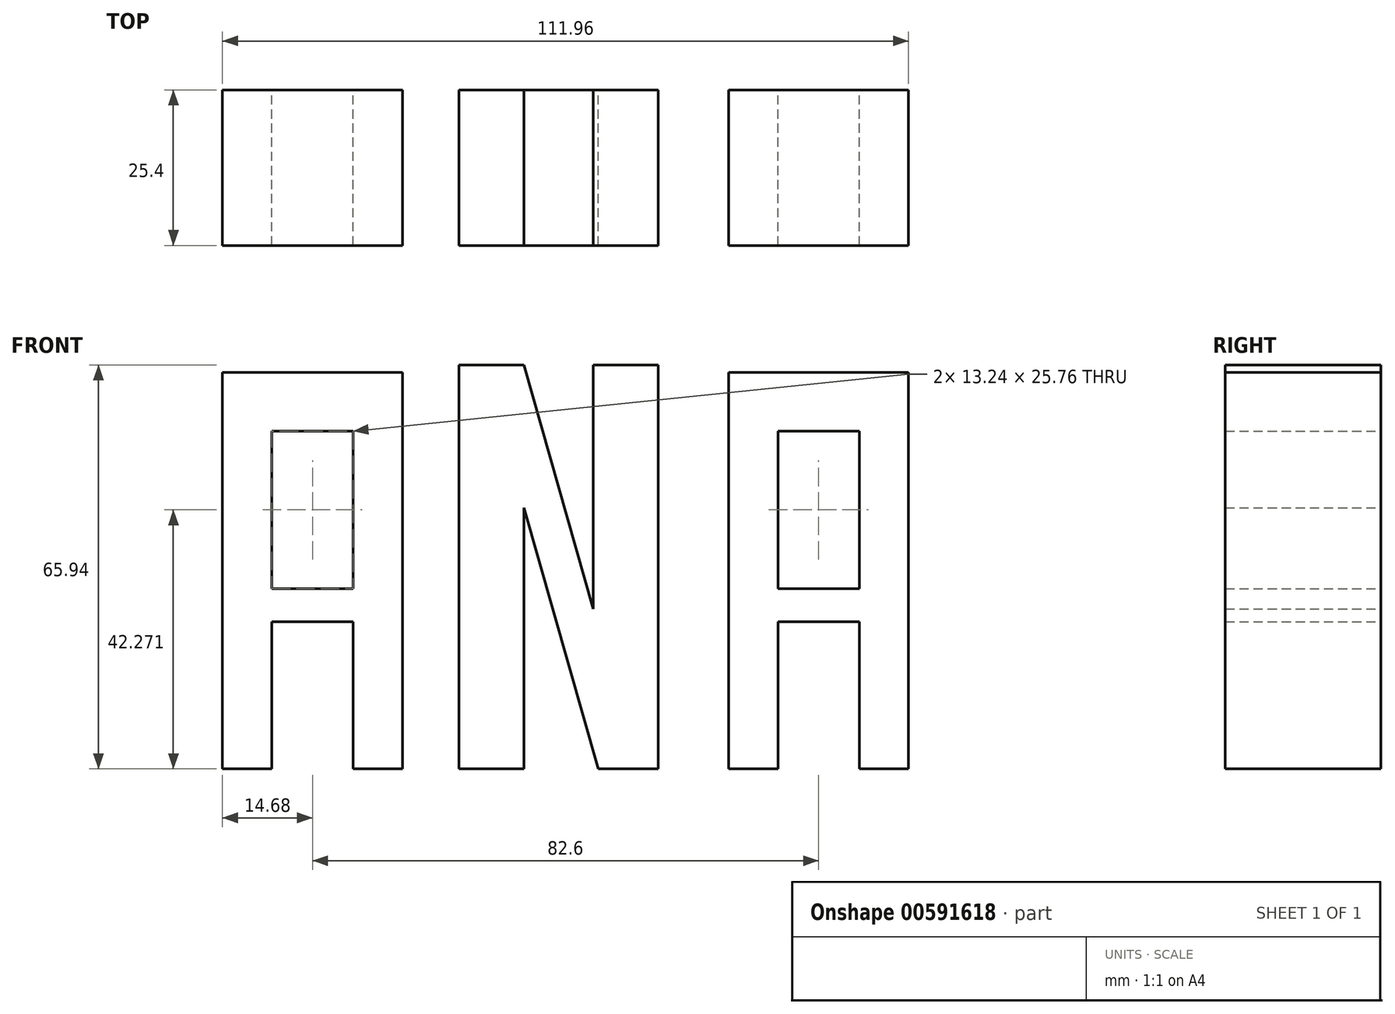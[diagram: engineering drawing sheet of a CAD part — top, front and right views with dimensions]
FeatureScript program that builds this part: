
annotation { "Feature Type Name" : "Feature", "Feature Type Description" : "" }
export const myFeature = defineFeature(function(context is Context, id is Id, definition is map)
    precondition{}
    {
        {
            var Q0;
            Q0=qCreatedBy(makeId("Front.planeOp"),FACE);
            var sketch = newSketch(context, id + "F0", { "sketchPlane" : qUnion([Q0])});
            skLineSegment(sketch, "E0", {"start": v(-55.98, 9.56) * mm, "end": v(-55.98, -55.15) * mm});
            skLineSegment(sketch, "E1", {"start": v(-55.98, -55.15) * mm, "end": v(-47.92, -55.15) * mm});
            skLineSegment(sketch, "E2", {"start": v(-47.92, -55.15) * mm, "end": v(-47.92, -7.12) * mm});
            skLineSegment(sketch, "E3.MirrorCS", {"start": v(-34.68, -55.15) * mm, "end": v(-34.68, -7.12) * mm});
            skLineSegment(sketch, "E4.MirrorCS", {"start": v(-26.62, -55.15) * mm, "end": v(-34.68, -55.15) * mm});
            skLineSegment(sketch, "E5.MirrorCS", {"start": v(-26.62, 9.56) * mm, "end": v(-26.62, -55.15) * mm});
            skLineSegment(sketch, "E6", {"start": v(-55.98, 9.56) * mm, "end": v(-26.62, 9.56) * mm});
            skLineSegment(sketch, "E7", {"start": v(-47.92, -31.14) * mm, "end": v(-34.68, -31.14) * mm});
            skLineSegment(sketch, "E8", {"start": v(-34.68, -31.14) * mm, "end": v(-34.68, -39.28) * mm});
            skLineSegment(sketch, "E9", {"start": v(-47.92, -7.12) * mm, "end": v(-47.92, 0) * mm});
            skLineSegment(sketch, "E10", {"start": v(-34.68, -7.12) * mm, "end": v(-34.68, 0) * mm});
            skLineSegment(sketch, "E11", {"start": v(-34.68, 0) * mm, "end": v(-47.92, 0) * mm});
            skLineSegment(sketch, "E12", {"start": v(-47.92, -25.76) * mm, "end": v(-34.68, -25.76) * mm});
            skLineSegment(sketch, "E13", {"start": v(-17.41, 9.07) * mm, "end": v(-17.41, -55.11) * mm});
            skLineSegment(sketch, "E14", {"start": v(-17.41, -55.11) * mm, "end": v(-6.76, -55.11) * mm});
            skLineSegment(sketch, "E15", {"start": v(-6.76, -55.11) * mm, "end": v(-6.76, -12.52) * mm});
            skLineSegment(sketch, "E16", {"start": v(-6.76, -12.52) * mm, "end": v(5.32, -55.11) * mm});
            skLineSegment(sketch, "E17", {"start": v(5.32, -55.11) * mm, "end": v(15.1, -55.11) * mm});
            skLineSegment(sketch, "E18", {"start": v(15.1, -55.11) * mm, "end": v(15.1, 10.8) * mm});
            skLineSegment(sketch, "E19", {"start": v(15.1, 10.8) * mm, "end": v(4.54, 10.8) * mm});
            skLineSegment(sketch, "E20", {"start": v(4.54, 10.8) * mm, "end": v(4.54, -29.05) * mm});
            skLineSegment(sketch, "E21", {"start": v(4.54, -29.05) * mm, "end": v(-6.76, 10.8) * mm});
            skLineSegment(sketch, "E22", {"start": v(-17.41, 10.8) * mm, "end": v(-17.41, 0) * mm});
            skLineSegment(sketch, "E23", {"start": v(-17.41, 10.8) * mm, "end": v(-6.76, 10.8) * mm});
            skLineSegment(sketch, "E24.MirrorCS", {"start": v(26.62, 9.56) * mm, "end": v(26.62, -55.15) * mm});
            skLineSegment(sketch, "E25.MirrorCS", {"start": v(55.98, 9.56) * mm, "end": v(26.62, 9.56) * mm});
            skLineSegment(sketch, "E26.MirrorCS", {"start": v(34.68, 0) * mm, "end": v(47.92, 0) * mm});
            skLineSegment(sketch, "E27.MirrorCS", {"start": v(55.98, 9.56) * mm, "end": v(55.98, -55.15) * mm});
            skLineSegment(sketch, "E28.MirrorCS", {"start": v(34.68, -55.15) * mm, "end": v(34.68, -7.12) * mm});
            skLineSegment(sketch, "E29.MirrorCS", {"start": v(47.92, -55.15) * mm, "end": v(47.92, -7.12) * mm});
            skLineSegment(sketch, "E30.MirrorCS", {"start": v(47.92, -7.12) * mm, "end": v(47.92, 0) * mm});
            skLineSegment(sketch, "E31.MirrorCS", {"start": v(34.68, -7.12) * mm, "end": v(34.68, 0) * mm});
            skLineSegment(sketch, "E32.MirrorCS", {"start": v(47.92, -25.76) * mm, "end": v(34.68, -25.76) * mm});
            skLineSegment(sketch, "E33.MirrorCS", {"start": v(47.92, -31.14) * mm, "end": v(34.68, -31.14) * mm});
            skLineSegment(sketch, "E34.MirrorCS", {"start": v(26.62, -55.15) * mm, "end": v(34.68, -55.15) * mm});
            skLineSegment(sketch, "E35.MirrorCS", {"start": v(55.98, -55.15) * mm, "end": v(47.92, -55.15) * mm});
            skSolve(sketch);
        }
        {
            var Q0;
            Q0 = qSketchRegion(id + "F0", true);
            extrude(context, id + "F1", {"entities" : qUnion([Q0]), "depth" : 25.4 * mm, "offsetDistance" : 25.4 * mm});
        }
    });
